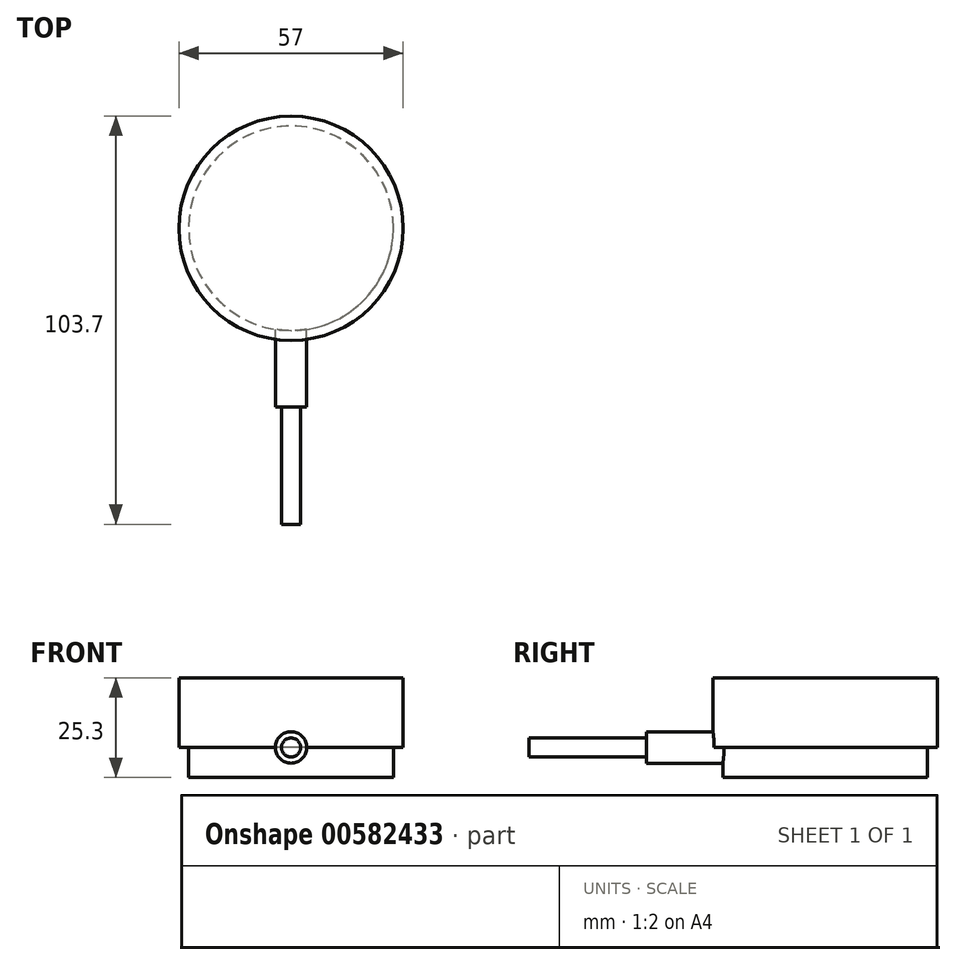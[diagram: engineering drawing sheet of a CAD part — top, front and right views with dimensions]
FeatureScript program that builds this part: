
annotation { "Feature Type Name" : "Feature", "Feature Type Description" : "" }
export const myFeature = defineFeature(function(context is Context, id is Id, definition is map)
    precondition{}
    {
        {
            var Q0;
            Q0=qCreatedBy(makeId("Top.planeOp"),FACE);
            var sketch = newSketch(context, id + "F0", { "sketchPlane" : qUnion([Q0])});
            skCircle(sketch, "E0", {"center": v(0, 0) * mm, "radius": 26 * mm});
            skSolve(sketch);
        }
        {
            var Q0;
            Q0 = qSketchRegion(id + "F0", true);
            extrude(context, id + "F1", {"entities" : qUnion([Q0]), "oppositeDirection" : true, "depth" : 7.6 * mm, "offsetDistance" : 25 * mm});
        }
        {
            var Q0;
            Q0=qCreatedBy(makeId("Top.planeOp"),FACE);
            cPlane(context, id + "F2", {"entities" : qUnion([Q0]), "cplaneType" : CPlaneType.OFFSET, "offset" : 17.7 * mm, "width" : 150 * mm, "height" : 150 * mm});
        }
        {
            var Q0;
            Q0=qCreatedBy(id+"F2.planeOp",FACE);
            var sketch = newSketch(context, id + "F3", { "sketchPlane" : qUnion([Q0])});
            skCircle(sketch, "E1", {"center": v(0, 0) * mm, "radius": 28.5 * mm});
            skSolve(sketch);
        }
        {
            var Q0;
            Q0=makeQuery(id+"F3.imprint","IMPRINT",FACE,{"disambiguationData":[TD([[makeQuery(id+"F3.imprint","IMPRINT",EDGE,{"derivedFrom":sQuery(id+"F3.wireOp",EDGE,"E1")}),1.0]])]});
            var Q1;
            Q1=qCreatedBy(makeId("Top.planeOp"),FACE);
            extrude(context, id + "F4", {"entities" : qUnion([Q0]), "operationType" : NewBodyOperationType.ADD, "endBound" : BoundingType.UP_TO_SURFACE, "oppositeDirection" : true, "depth" : 25 * mm, "endBoundEntityFace" : qUnion([Q1]), "offsetDistance" : 25 * mm});
        }
        {
            var Q0;
            Q0=qCreatedBy(makeId("Front.planeOp"),FACE);
            cPlane(context, id + "F5", {"entities" : qUnion([Q0]), "cplaneType" : CPlaneType.OFFSET, "offset" : ((57 / 2) + 16.9) * mm, "width" : 150 * mm, "height" : 150 * mm});
        }
        {
            var Q0;
            Q0=qCreatedBy(makeId("Front.planeOp"),FACE);
            var sketch = newSketch(context, id + "F6", { "sketchPlane" : qUnion([Q0])});
            skCircle(sketch, "E2", {"center": v(0, 0) * mm, "radius": 4 * mm});
            skSolve(sketch);
        }
        {
            var Q0;
            Q0 = qSketchRegion(id + "F6", true);
            var Q1;
            Q1=qCreatedBy(id+"F5.planeOp",FACE);
            extrude(context, id + "F7", {"entities" : qUnion([Q0]), "operationType" : NewBodyOperationType.ADD, "endBound" : BoundingType.UP_TO_SURFACE, "depth" : 25 * mm, "endBoundEntityFace" : qUnion([Q1]), "offsetDistance" : 25 * mm});
        }
        {
            var Q0;
            Q0=qCreatedBy(makeId("Front.planeOp"),FACE);
            cPlane(context, id + "F8", {"entities" : qUnion([Q0]), "cplaneType" : CPlaneType.OFFSET, "offset" : 75.2 * mm, "width" : 150 * mm, "height" : 150 * mm});
        }
        {
            var Q0;
            Q0=makeQuery(id+"F7.opExtrude","CAP_FACE",FACE,{"disambiguationData":[OSD([sQuery(id+"F6.wireOp",EDGE,"E2")])],"isStart":false});
            var sketch = newSketch(context, id + "F9", { "sketchPlane" : qUnion([Q0])});
            skCircle(sketch, "E3", {"center": v(0, 0) * mm, "radius": 2.4 * mm});
            skSolve(sketch);
        }
        {
            var Q0;
            Q0 = qSketchRegion(id + "F9", true);
            var Q1;
            Q1=qCreatedBy(id+"F8.planeOp",FACE);
            extrude(context, id + "F10", {"entities" : qUnion([Q0]), "operationType" : NewBodyOperationType.ADD, "endBound" : BoundingType.UP_TO_SURFACE, "depth" : 25 * mm, "endBoundEntityFace" : qUnion([Q1]), "offsetDistance" : 25 * mm});
        }
    });
